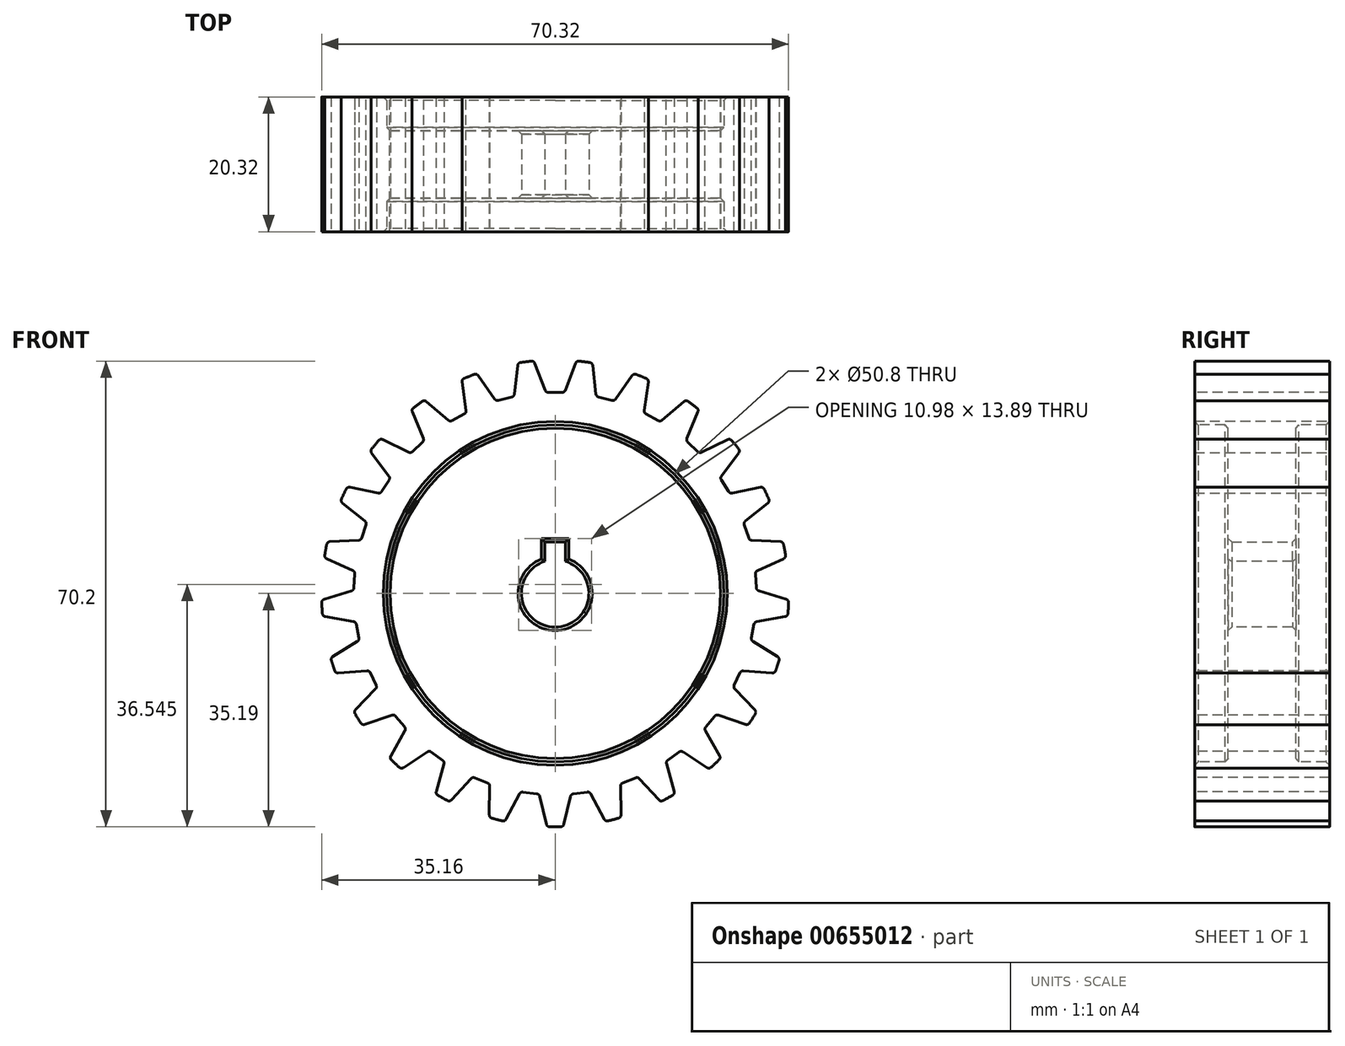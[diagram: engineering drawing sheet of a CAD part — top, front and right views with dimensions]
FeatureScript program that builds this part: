
annotation { "Feature Type Name" : "Feature", "Feature Type Description" : "" }
export const myFeature = defineFeature(function(context is Context, id is Id, definition is map)
    precondition{}
    {
        {
            var Q0;
            Q0=qCreatedBy(makeId("Right.planeOp"),FACE);
            var sketch = newSketch(context, id + "F0", { "sketchPlane" : qUnion([Q0])});
            skLineSegment(sketch, "E0", {"start": v(0, 0) * mm, "end": v(16.6, 0) * mm});
            skLineSegment(sketch, "E1", {"start": v(0, 0) * mm, "end": v(0, 25.4) * mm});
            skLineSegment(sketch, "E2", {"start": v(0, 25.4) * mm, "end": v(10.16, 25.4) * mm});
            skLineSegment(sketch, "E3", {"start": v(-10.16, 25.4) * mm, "end": v(0, 25.4) * mm});
            skLineSegment(sketch, "E4", {"start": v(0, 0) * mm, "end": v(0, 5.08) * mm});
            skLineSegment(sketch, "E5", {"start": v(0, 5.08) * mm, "end": v(5.08, 5.08) * mm});
            skLineSegment(sketch, "E6", {"start": v(5.08, 5.08) * mm, "end": v(5.08, 25.4) * mm});
            skLineSegment(sketch, "E7", {"start": v(0, 5.08) * mm, "end": v(-5.08, 5.08) * mm});
            skLineSegment(sketch, "E8", {"start": v(-5.08, 5.08) * mm, "end": v(-5.08, 25.4) * mm});
            skPoint(sketch, "E8.endSnap0", {"position": v(-7.62, 25.4) * mm});
            skLineSegment(sketch, "E9", {"start": v(0, 35.2) * mm, "end": v(0, 25.4) * mm});
            skPoint(sketch, "E10.orphan", {"position": v(15.24, 35.2) * mm});
            skPoint(sketch, "E11.end.orphan", {"position": v(-15.24, 35.2) * mm});
            skLineSegment(sketch, "E12", {"start": v(0, 35.2) * mm, "end": v(-10.16, 35.2) * mm});
            skLineSegment(sketch, "E13", {"start": v(0, 35.2) * mm, "end": v(10.16, 35.2) * mm});
            skLineSegment(sketch, "E14", {"start": v(10.16, 35.2) * mm, "end": v(10.16, 25.4) * mm});
            skLineSegment(sketch, "E15", {"start": v(-10.16, 35.2) * mm, "end": v(-10.16, 25.4) * mm});
            skPoint(sketch, "E16.orphan", {"position": v(-15.24, 25.4) * mm});
            skSolve(sketch);
        }
        {
            var Q0;
            Q0=makeQuery(id+"F0.imprint","IMPRINT",FACE,{"disambiguationData":[TD([[makeQuery(id+"F0.imprint","IMPRINT",EDGE,{"derivedFrom":sQuery(id+"F0.wireOp",EDGE,"E2")}),1.0]])]});
            var Q1;
            {var subQ0=sQuery(id+"F0.wireOp",EDGE,"E1");Q1=makeQuery(id+"F0.imprint","IMPRINT",FACE,{"disambiguationData":[TD([[makeQuery(id+"F0.imprint","IMPRINT",EDGE,{"derivedFrom":subQ0}),1.0]])]});}
            var Q2;
            {var subQ0=sQuery(id+"F0.wireOp",EDGE,"E1");Q2=makeQuery(id+"F0.imprint","IMPRINT",FACE,{"disambiguationData":[TD([[makeQuery(id+"F0.imprint","IMPRINT",EDGE,{"derivedFrom":subQ0}),-1.0]])]});}
            var Q3;
            {var subQ0=sQuery(id+"F0.wireOp",EDGE,"E9");Q3=makeQuery(id+"F0.imprint","IMPRINT",FACE,{"disambiguationData":[TD([[makeQuery(id+"F0.imprint","IMPRINT",EDGE,{"derivedFrom":subQ0}),-1.0]])]});}
            var Q4;
            Q4=sQuery(id+"F0.wireOp",EDGE,"E0");
            revolve(context, id + "F1", {"entities" : qUnion([Q0, Q1, Q2, Q3]), "axis" : qUnion([Q4]), "revolveType" : RevolveType.FULL});
        }
        {
            var Q0;
            Q0=qCreatedBy(makeId("Front.planeOp"),FACE);
            var sketch = newSketch(context, id + "F2", { "sketchPlane" : qUnion([Q0])});
            skLineSegment(sketch, "E17", {"start": v(0, 35.3) * mm, "end": v(3.3, 35.3) * mm});
            skLineSegment(sketch, "E18", {"start": v(0, 30.3) * mm, "end": v(1.4, 30.3) * mm});
            skLineSegment(sketch, "E19", {"start": v(1.4, 30.3) * mm, "end": v(3.3, 35.3) * mm});
            skLineSegment(sketch, "E20.MirrorCS", {"start": v(0, 30.3) * mm, "end": v(-1.4, 30.3) * mm});
            skLineSegment(sketch, "E21.MirrorCS", {"start": v(0, 35.3) * mm, "end": v(-3.3, 35.3) * mm});
            skLineSegment(sketch, "E22.MirrorCS", {"start": v(-1.4, 30.3) * mm, "end": v(-3.3, 35.3) * mm});
            skSolve(sketch);
        }
        {
            var Q0;
            Q0 = qSketchRegion(id + "F2", true);
            extrude(context, id + "F3", {"entities" : qUnion([Q0]), "operationType" : NewBodyOperationType.REMOVE, "endBound" : BoundingType.SYMMETRIC, "oppositeDirection" : true, "depth" : 25.4 * mm, "offsetDistance" : 25.4 * mm});
        }
        {
            var Q0;
            Q0=makeQuery(id+"F3.boolean.opBoolean","COPY",EDGE,{"derivedFrom":makeQuery(id+"F3.opExtrude","SWEPT_EDGE",EDGE,{"disambiguationData":[OSD([sQuery(id+"F2.wireOp",EDGE,"E20.MirrorCS"),sQuery(id+"F2.wireOp",EDGE,"E22.MirrorCS")])]})});
            var Q1;
            Q1=makeQuery(id+"F3.boolean.opBoolean","COPY",EDGE,{"derivedFrom":makeQuery(id+"F3.opExtrude","SWEPT_EDGE",EDGE,{"disambiguationData":[OSD([sQuery(id+"F2.wireOp",EDGE,"E18"),sQuery(id+"F2.wireOp",EDGE,"E19")])]})});
            var Q2;
            Q2=makeQuery(id+"F3.boolean.opBoolean","INTERSECT",EDGE,{"derivedFrom":[makeQuery(id+"F1.opRevolve","SWEPT_FACE",FACE,{"disambiguationData":[OSD([sQuery(id+"F0.wireOp",EDGE,"E12"),sQuery(id+"F0.wireOp",EDGE,"E13")])]}),makeQuery(id+"F3.opExtrude","SWEPT_FACE",FACE,{"disambiguationData":[OSD([sQuery(id+"F2.wireOp",EDGE,"E19")])]})]});
            var Q3;
            Q3=makeQuery(id+"F3.boolean.opBoolean","INTERSECT",EDGE,{"derivedFrom":[makeQuery(id+"F1.opRevolve","SWEPT_FACE",FACE,{"disambiguationData":[OSD([sQuery(id+"F0.wireOp",EDGE,"E12"),sQuery(id+"F0.wireOp",EDGE,"E13")])]}),makeQuery(id+"F3.opExtrude","SWEPT_FACE",FACE,{"disambiguationData":[OSD([sQuery(id+"F2.wireOp",EDGE,"E22.MirrorCS")])]})]});
            fillet(context, id + "F4", {"entities" : qUnion([Q0, Q1, Q2, Q3]), "radius" : 0.5 * mm, "tangentPropagation" : true, "allowEdgeOverflow" : false});
        }
        {
            var Q0;
            Q0=makeQuery(id+"F3.boolean.opBoolean","COPY",FACE,{"derivedFrom":makeQuery(id+"F3.opExtrude","SWEPT_FACE",FACE,{"disambiguationData":[OSD([sQuery(id+"F2.wireOp",EDGE,"E19")])]})});
            var Q1;
            Q1=makeQuery(id+"F3.boolean.opBoolean","COPY",FACE,{"derivedFrom":makeQuery(id+"F3.opExtrude","SWEPT_FACE",FACE,{"disambiguationData":[OSD([sQuery(id+"F2.wireOp",EDGE,"E18"),sQuery(id+"F2.wireOp",EDGE,"E20.MirrorCS")])]})});
            var Q2;
            Q2=makeQuery(id+"F3.boolean.opBoolean","COPY",FACE,{"derivedFrom":makeQuery(id+"F3.opExtrude","SWEPT_FACE",FACE,{"disambiguationData":[OSD([sQuery(id+"F2.wireOp",EDGE,"E22.MirrorCS")])]})});
            var Q3;
            Q3=makeQuery(id+"F4.opFillet","BLEND_FACE",FACE,{"disambiguationData":[OSD([sQuery(id+"F0.wireOp",EDGE,"E12"),sQuery(id+"F0.wireOp",EDGE,"E13"),sQuery(id+"F2.wireOp",EDGE,"E22.MirrorCS")])]});
            var Q4;
            Q4=makeQuery(id+"F4.opFillet","BLEND_FACE",FACE,{"disambiguationData":[OSD([sQuery(id+"F2.wireOp",EDGE,"E20.MirrorCS"),sQuery(id+"F2.wireOp",EDGE,"E22.MirrorCS")])]});
            var Q5;
            Q5=makeQuery(id+"F4.opFillet","BLEND_FACE",FACE,{"disambiguationData":[OSD([sQuery(id+"F2.wireOp",EDGE,"E18"),sQuery(id+"F2.wireOp",EDGE,"E19")])]});
            var Q6;
            Q6=makeQuery(id+"F4.opFillet","BLEND_FACE",FACE,{"disambiguationData":[OSD([sQuery(id+"F0.wireOp",EDGE,"E12"),sQuery(id+"F0.wireOp",EDGE,"E13"),sQuery(id+"F2.wireOp",EDGE,"E19")])]});
            var Q7;
            Q7=makeQuery(id+"F1.opRevolve","SWEPT_FACE",FACE,{"disambiguationData":[OSD([sQuery(id+"F0.wireOp",EDGE,"E12"),sQuery(id+"F0.wireOp",EDGE,"E13")])]});
            circularPattern(context, id + "F5", {"patternType" : PatternType.FACE, "faces" : qUnion([Q0, Q1, Q2, Q3, Q4, Q5, Q6]), "axis" : qUnion([Q7]), "angle" : 360 * degree, "instanceCount" : 25, "equalSpace" : true});
        }
        {
            var Q0;
            Q0=qCreatedBy(makeId("Front.planeOp"),FACE);
            var sketch = newSketch(context, id + "F6", { "sketchPlane" : qUnion([Q0])});
            skLineSegment(sketch, "E23.bottom", {"start": v(-1.54, 7.8) * mm, "end": v(1.54, 7.8) * mm});
            skLineSegment(sketch, "E23.top", {"start": v(-1.54, 3.26) * mm, "end": v(1.54, 3.26) * mm});
            skLineSegment(sketch, "E23.left", {"start": v(-1.54, 7.8) * mm, "end": v(-1.54, 3.26) * mm});
            skLineSegment(sketch, "E23.right", {"start": v(1.54, 7.8) * mm, "end": v(1.54, 3.26) * mm});
            skPoint(sketch, "E23.middle", {"position": v(0, 0) * mm});
            skSolve(sketch);
        }
        {
            var Q0;
            Q0 = qSketchRegion(id + "F6", true);
            extrude(context, id + "F7", {"entities" : qUnion([Q0]), "operationType" : NewBodyOperationType.REMOVE, "endBound" : BoundingType.SYMMETRIC, "depth" : 25.4 * mm, "offsetDistance" : 25.4 * mm});
        }
        {
            var Q0;
            Q0=makeQuery(id+"F1.opRevolve","SWEPT_EDGE",EDGE,{"disambiguationData":[OSD([sQuery(id+"F0.wireOp",EDGE,"E3"),sQuery(id+"F0.wireOp",EDGE,"E8")])]});
            var Q1;
            Q1=makeQuery(id+"F1.opRevolve","SWEPT_EDGE",EDGE,{"disambiguationData":[OSD([sQuery(id+"F0.wireOp",EDGE,"E3"),sQuery(id+"F0.wireOp",EDGE,"E15")])]});
            var Q2;
            Q2=makeQuery(id+"F1.opRevolve","SWEPT_EDGE",EDGE,{"disambiguationData":[OSD([sQuery(id+"F0.wireOp",EDGE,"E2"),sQuery(id+"F0.wireOp",EDGE,"E6")])]});
            var Q3;
            Q3=makeQuery(id+"F1.opRevolve","SWEPT_EDGE",EDGE,{"disambiguationData":[OSD([sQuery(id+"F0.wireOp",EDGE,"E2"),sQuery(id+"F0.wireOp",EDGE,"E14")])]});
            var Q4;
            Q4=makeQuery(id+"F1.opRevolve","SWEPT_EDGE",EDGE,{"disambiguationData":[OSD([sQuery(id+"F0.wireOp",EDGE,"E7"),sQuery(id+"F0.wireOp",EDGE,"E8")])]});
            var Q5;
            Q5=makeQuery(id+"F7.boolean.opBoolean","INTERSECT",EDGE,{"derivedFrom":[makeQuery(id+"F1.opRevolve","SWEPT_FACE",FACE,{"disambiguationData":[OSD([sQuery(id+"F0.wireOp",EDGE,"E8")])]}),makeQuery(id+"F7.opExtrude","SWEPT_FACE",FACE,{"disambiguationData":[OSD([sQuery(id+"F6.wireOp",EDGE,"E23.left")])]})]});
            var Q6;
            Q6=makeQuery(id+"F7.boolean.opBoolean","INTERSECT",EDGE,{"derivedFrom":[makeQuery(id+"F1.opRevolve","SWEPT_FACE",FACE,{"disambiguationData":[OSD([sQuery(id+"F0.wireOp",EDGE,"E8")])]}),makeQuery(id+"F7.opExtrude","SWEPT_FACE",FACE,{"disambiguationData":[OSD([sQuery(id+"F6.wireOp",EDGE,"E23.bottom")])]})]});
            var Q7;
            Q7=makeQuery(id+"F7.boolean.opBoolean","INTERSECT",EDGE,{"derivedFrom":[makeQuery(id+"F1.opRevolve","SWEPT_FACE",FACE,{"disambiguationData":[OSD([sQuery(id+"F0.wireOp",EDGE,"E8")])]}),makeQuery(id+"F7.opExtrude","SWEPT_FACE",FACE,{"disambiguationData":[OSD([sQuery(id+"F6.wireOp",EDGE,"E23.right")])]})]});
            var Q8;
            Q8=makeQuery(id+"F1.opRevolve","SWEPT_EDGE",EDGE,{"disambiguationData":[OSD([sQuery(id+"F0.wireOp",EDGE,"E5"),sQuery(id+"F0.wireOp",EDGE,"E6")])]});
            var Q9;
            Q9=makeQuery(id+"F7.boolean.opBoolean","INTERSECT",EDGE,{"derivedFrom":[makeQuery(id+"F1.opRevolve","SWEPT_FACE",FACE,{"disambiguationData":[OSD([sQuery(id+"F0.wireOp",EDGE,"E6")])]}),makeQuery(id+"F7.opExtrude","SWEPT_FACE",FACE,{"disambiguationData":[OSD([sQuery(id+"F6.wireOp",EDGE,"E23.left")])]})]});
            var Q10;
            Q10=makeQuery(id+"F7.boolean.opBoolean","INTERSECT",EDGE,{"derivedFrom":[makeQuery(id+"F1.opRevolve","SWEPT_FACE",FACE,{"disambiguationData":[OSD([sQuery(id+"F0.wireOp",EDGE,"E6")])]}),makeQuery(id+"F7.opExtrude","SWEPT_FACE",FACE,{"disambiguationData":[OSD([sQuery(id+"F6.wireOp",EDGE,"E23.bottom")])]})]});
            var Q11;
            Q11=makeQuery(id+"F7.boolean.opBoolean","INTERSECT",EDGE,{"derivedFrom":[makeQuery(id+"F1.opRevolve","SWEPT_FACE",FACE,{"disambiguationData":[OSD([sQuery(id+"F0.wireOp",EDGE,"E6")])]}),makeQuery(id+"F7.opExtrude","SWEPT_FACE",FACE,{"disambiguationData":[OSD([sQuery(id+"F6.wireOp",EDGE,"E23.right")])]})]});
            chamfer(context, id + "F8", {"entities" : qUnion([Q0, Q1, Q2, Q3, Q4, Q5, Q6, Q7, Q8, Q9, Q10, Q11]), "width" : 0.5 * mm, "tangentPropagation" : true});
        }
    });
